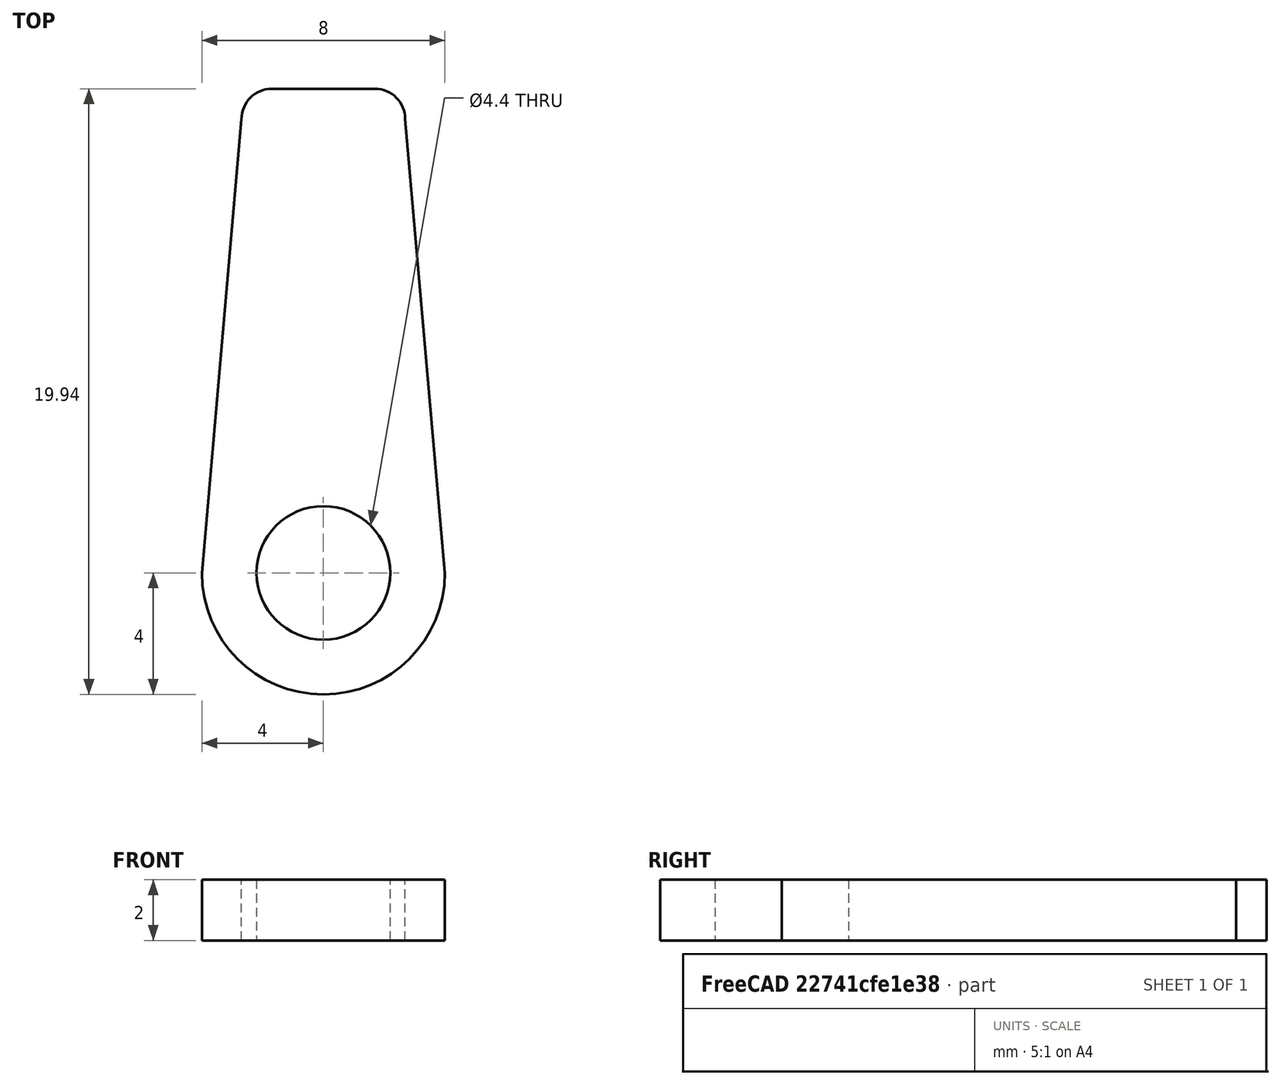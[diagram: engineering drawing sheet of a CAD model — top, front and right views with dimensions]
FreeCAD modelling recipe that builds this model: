
FCSTD DOCUMENT  (FreeCAD 0.19R23258 (Git))
Label: Printer-Paper-Slider
License: All rights reserved
LicenseURL: http://en.wikipedia.org/wiki/All_rights_reserved
objects: TechDraw::DrawViewDimension×6, TechDraw::DrawViewPart×2, Sketcher::SketchObject×1, PartDesign::Pad×1, PartDesign::Body×1, TechDraw::DrawSVGTemplate×1, TechDraw::DrawViewSymbol×1, TechDraw::DrawPage×1
note: 4 computed .brp shape members not serialized (recipe doc carries the construction recipe); baked Part::Feature solids carry a one-line shape summary decoded from their .brp

FEATURE [Sketcher::SketchObject] Sketch
  MapMode = 5
  Support = -> [XY_Plane]
  sketch-geometry (8):
    g0: Circle CenterX=0 CenterY=0 CenterZ=0 NormalX=0 NormalY=0 NormalZ=1 AngleXU=0 Radius=2.2
    g1: ArcOfCircle CenterX=0 CenterY=0 CenterZ=0 NormalX=0 NormalY=0 NormalZ=1 AngleXU=0 Radius=4 StartAngle=3.14159 EndAngle=6.28319
    g2: LineSegment StartX=-4 StartY=5e-16 StartZ=0 EndX=-2.69266 EndY=14.9429 EndZ=0
    g3: ArcOfCircle CenterX=-1.69266 CenterY=14.9429 CenterZ=0 NormalX=0 NormalY=0 NormalZ=1 AngleXU=0 Radius=1 StartAngle=1.5708 EndAngle=3.14159
    g4: LineSegment StartX=-1.69266 StartY=15.9429 StartZ=0 EndX=0 EndY=15.9429 EndZ=0
    g5: ArcOfCircle CenterX=1.69266 CenterY=14.9429 CenterZ=0 NormalX=0 NormalY=0 NormalZ=1 AngleXU=0 Radius=1 StartAngle=0 EndAngle=1.5708
    g6: LineSegment StartX=1.69266 StartY=15.9429 StartZ=0 EndX=0 EndY=15.9429 EndZ=0
    g7: LineSegment StartX=2.69266 StartY=14.9429 StartZ=0 EndX=4 EndY=-1.8e-15 EndZ=0
  constraints (25):
    c: Coincident(g0,g-1)
    c: Diameter(g0) = 4.4
    c: Coincident(g1,g0)
    c: PointOnObject(g1,g-1)
    c: PointOnObject(g1,g-1)
    c: Diameter(g1) = 8
    c: Coincident(g2,g1)
    c: Distance(g2) = 15
    c: Coincident(g3,g2)
    c: Coincident(g4,g3)
    c: PointOnObject(g4,g-2)
    c: Horizontal(g4)
    c: Diameter(g3) = 2
    c: Angle(g-1,g2) = 1.48353
    c: Horizontal(g2,g3)
    c: Vertical(g3,g3)
    c: Coincident(g6,g5)
    c: Horizontal(g6)
    c: Diameter(g5) = 2
    c: Equal(g4,g6)
    c: Coincident(g4,g6)
    c: Horizontal(g2,g5)
    c: Vertical(g5,g5)
    c: Coincident(g7,g5)
    c: Coincident(g7,g1)
FEATURE [PartDesign::Pad] Pad
  Direction = (1,1,1)
  Length = 2
  Length2 = 100
  Profile = -> Sketch
  Type = 0
FEATURE [PartDesign::Body] Body
  Group = -> [Sketch,Pad]
  Origin = -> Origin
  Tip = -> Pad
FEATURE [TechDraw::DrawSVGTemplate] Template
  EditableTexts = Designed_by_Name=Designed by Name; Drawing_number=Drawing number; FC-Date=Date; FC-SC=Scale 3; FC-SH=Sheet; FC-Title=Title; Subtitle=Subtitle; Weight=Weight
  Height = 210
  Orientation = 1
  Width = 297
FEATURE [TechDraw::DrawViewPart] View  label="Top view"
  CoarseView = false
  Direction = (0,0,1)
  Focus = 100
  HardHidden = false
  IsoCount = 0
  IsoHidden = false
  IsoVisible = false
  LockPosition = false
  Perspective = false
  Rotation = 0
  Scale = 3
  ScaleType = 0
  SeamHidden = false
  SeamVisible = true
  SmoothHidden = false
  SmoothVisible = true
  Source = -> [Pad]
  X = 73.8974
  XDirection = (1,0,0)
  Y = 138.318
FEATURE [TechDraw::DrawViewDimension] Dimension
  Arbitrary = false
  ArbitraryTolerances = false
  FormatSpec = ⌀%.2f
  FormatSpecOverTolerance = %+g
  FormatSpecUnderTolerance = %+g
  Inverted = false
  LockPosition = false
  MeasureType = 1
  OverTolerance = 0
  References2D = -> [View]
  Rotation = 0
  Scale = 3
  ScaleType = 0
  TheoreticalExact = false
  Type = 5
  UnderTolerance = 0
  X = -25.1887
  Y = -28.2527
FEATURE [TechDraw::DrawViewDimension] Dimension001
  Arbitrary = false
  ArbitraryTolerances = false
  FormatSpec = ⌀%.2f
  FormatSpecOverTolerance = %+g
  FormatSpecUnderTolerance = %+g
  Inverted = false
  LockPosition = false
  MeasureType = 1
  OverTolerance = 0
  References2D = -> [View]
  Rotation = 0
  Scale = 3
  ScaleType = 0
  TheoreticalExact = false
  Type = 5
  UnderTolerance = 0
  X = 24.8769
  Y = -28.0958
FEATURE [TechDraw::DrawViewDimension] Dimension002
  Arbitrary = false
  ArbitraryTolerances = false
  FormatSpec = %.2f
  FormatSpecOverTolerance = %+g
  FormatSpecUnderTolerance = %+g
  Inverted = false
  LockPosition = false
  MeasureType = 1
  OverTolerance = 0
  References2D = -> [View]
  Rotation = 0
  Scale = 3
  ScaleType = 0
  TheoreticalExact = false
  Type = 0
  UnderTolerance = 0
  X = 27.0047
  Y = 5.97037
FEATURE [TechDraw::DrawViewPart] View001  label="Side View"
  CoarseView = false
  Direction = (1,0,0)
  Focus = 100
  HardHidden = false
  IsoCount = 0
  IsoHidden = false
  IsoVisible = false
  LockPosition = false
  Perspective = false
  Rotation = 0
  Scale = 3
  ScaleType = 0
  SeamHidden = false
  SeamVisible = true
  SmoothHidden = false
  SmoothVisible = true
  Source = -> [Body]
  X = 77.4848
  XDirection = (0,1,0)
  Y = 56.011
FEATURE [TechDraw::DrawViewDimension] Dimension003
  Arbitrary = false
  ArbitraryTolerances = false
  FormatSpec = %.2f
  FormatSpecOverTolerance = %+g
  FormatSpecUnderTolerance = %+g
  Inverted = false
  LockPosition = false
  MeasureType = 1
  OverTolerance = 0
  References2D = -> [View001]
  Rotation = 0
  Scale = 3
  ScaleType = 0
  TheoreticalExact = false
  Type = 2
  UnderTolerance = 0
  X = 30.2986
  Y = 17.2756
FEATURE [TechDraw::DrawViewDimension] Dimension004
  Arbitrary = false
  ArbitraryTolerances = false
  FormatSpec = ⌀%.2f
  FormatSpecOverTolerance = %+g
  FormatSpecUnderTolerance = %+g
  Inverted = false
  LockPosition = false
  MeasureType = 1
  OverTolerance = 0
  References2D = -> [View]
  Rotation = 0
  Scale = 3
  ScaleType = 0
  TheoreticalExact = false
  Type = 5
  UnderTolerance = 0
  X = 25.0869
  Y = 36.2989
FEATURE [TechDraw::DrawViewDimension] Dimension005
  Arbitrary = false
  ArbitraryTolerances = false
  FormatSpec = %.2f
  FormatSpecOverTolerance = %+g
  FormatSpecUnderTolerance = %+g
  Inverted = false
  LockPosition = false
  MeasureType = 1
  OverTolerance = 0
  References2D = -> [View]
  Rotation = 0
  Scale = 3
  ScaleType = 0
  TheoreticalExact = false
  Type = 1
  UnderTolerance = 0
  X = 15.6778
  Y = 46.0851
FEATURE [TechDraw::DrawViewSymbol] ActiveView  label="3D View"
  LockPosition = false
  Rotation = 0
  Scale = 0.3
  ScaleType = 2
  Symbol = <blob: 15885 chars omitted>
  X = 199.754
  Y = 140.878
FEATURE [TechDraw::DrawPage] Page
  KeepUpdated = true
  NextBalloonIndex = 1
  ProjectionType = 0
  Scale = 3
  Template = -> Template
  Views = -> [View,Dimension,Dimension001,Dimension002,View001,Dimension003,Dimension004,Dimension005,ActiveView]
